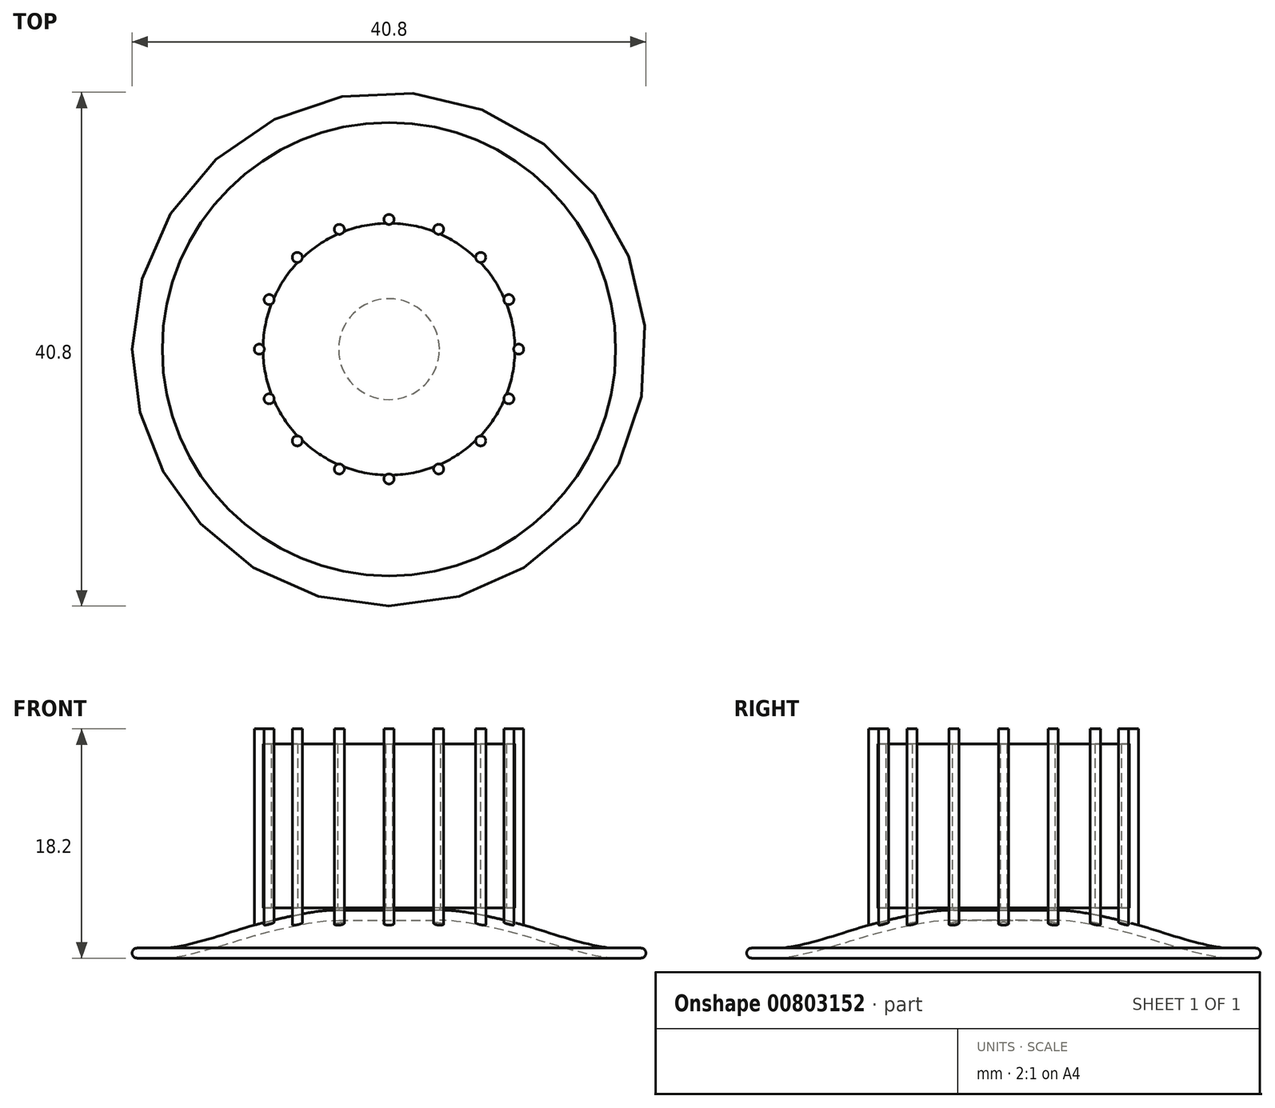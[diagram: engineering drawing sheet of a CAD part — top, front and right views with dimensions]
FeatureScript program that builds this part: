
annotation { "Feature Type Name" : "Feature", "Feature Type Description" : "" }
export const myFeature = defineFeature(function(context is Context, id is Id, definition is map)
    precondition{}
    {
        {
            var Q0;
            Q0=qCreatedBy(makeId("Right.planeOp"),FACE);
            var sketch = newSketch(context, id + "F0", { "sketchPlane" : qUnion([Q0])});
            skPoint(sketch, "E0", {"position": v(0, 3) * mm});
            skPoint(sketch, "E1", {"position": v(-4, 3) * mm});
            skPoint(sketch, "E2", {"position": v(-18, 0) * mm});
            skLineSegment(sketch, "E3", {"start": v(-4, 3) * mm, "end": v(0, 3) * mm});
            skLineSegment(sketch, "E4", {"start": v(-18, 0) * mm, "end": v(-20, 0) * mm});
            skFitSpline(sketch, "E5", {"points": [v(-18, 0) * mm, v(-14.38, 0.68) * mm, v(-10.9, 1.72) * mm, v(-7.39, 2.59) * mm, v(-4, 3) * mm], "startDerivative": vector(11.3, 0) * mm, "endDerivative": vector(14.02, 0) * mm});
            skLineSegment(sketch, "E6.bottom", {"start": v(0, 3) * mm, "end": v(-4, 3) * mm});
            skLineSegment(sketch, "E6.top", {"start": v(0, 4) * mm, "end": v(-4, 4) * mm});
            skLineSegment(sketch, "E6.left", {"start": v(0, 3) * mm, "end": v(0, 4) * mm});
            skLineSegment(sketch, "E6.right", {"start": v(-4, 3) * mm, "end": v(-4, 4) * mm});
            skPoint(sketch, "E7", {"position": v(-20, 0.8) * mm});
            skArc(sketch, "E8", {"start": v(-20, 0.8) * mm, "mid": v(-20.4, 0.4) * mm, "end": v(-20, 0) * mm});
            skFitSpline(sketch, "E9.0", {"points": [v(-18, 0.8) * mm, v(-17.81, 0.8) * mm, v(-17.35, 0.83) * mm, v(-16.22, 1.03) * mm, v(-14.61, 1.43) * mm, v(-12.89, 1.95) * mm, v(-11.2, 2.47) * mm, v(-9.43, 2.95) * mm, v(-7.93, 3.3) * mm, v(-6.74, 3.53) * mm, v(-5.55, 3.72) * mm, v(-4.63, 3.8) * mm, v(-4, 3.8) * mm]});
            skLineSegment(sketch, "E9.1", {"start": v(-18, 0.8) * mm, "end": v(-20, 0.8) * mm});
            skLineSegment(sketch, "E10.bottom", {"start": v(0, 4) * mm, "end": v(-10, 4) * mm});
            skLineSegment(sketch, "E10.top", {"start": v(0, 17) * mm, "end": v(-10, 17) * mm});
            skLineSegment(sketch, "E10.left", {"start": v(0, 4) * mm, "end": v(0, 17) * mm});
            skLineSegment(sketch, "E10.right", {"start": v(-10, 4) * mm, "end": v(-10, 17) * mm});
            skPoint(sketch, "E11", {"position": v(-10, 2.2) * mm});
            skPoint(sketch, "E12", {"position": v(-10.8, 2.2) * mm});
            skSolve(sketch);
        }
        {
            var Q0;
            Q0=makeQuery(id+"F0.imprint","IMPRINT",FACE,{"disambiguationData":[TD([[makeQuery(id+"F0.imprint","IMPRINT",EDGE,{"derivedFrom":sQuery(id+"F0.wireOp",EDGE,"E4")}),-1.0]])]});
            var Q1;
            {var subQ2=sQuery(id+"F0.wireOp",EDGE,"E3");Q1=makeQuery(id+"F0.imprint","IMPRINT",FACE,{"disambiguationData":[TD([[makeQuery(id+"F0.imprint","IMPRINT",EDGE,{"derivedFrom":subQ2}),1.0]])]});}
            var Q2;
            Q2=makeQuery(id+"F0.imprint","IMPRINT",FACE,{"disambiguationData":[TD([[makeQuery(id+"F0.imprint","IMPRINT",EDGE,{"derivedFrom":sQuery(id+"F0.wireOp",EDGE,"E6.top")}),-1.0]])]});
            var Q3;
            Q3=sQuery(id+"F0.wireOp",EDGE,"E6.left");
            revolve(context, id + "F1", {"surfaceOperationType" : NewSurfaceOperationType.NEW, "entities" : qUnion([Q0, Q1, Q2]), "axis" : qUnion([Q3]), "revolveType" : RevolveType.FULL});
        }
        {
            var Q0;
            Q0=qCreatedBy(makeId("Top.planeOp"),FACE);
            cPlane(context, id + "F2", {"entities" : qUnion([Q0]), "cplaneType" : CPlaneType.OFFSET, "offset" : 2.2 * mm, "width" : 150 * mm, "height" : 150 * mm});
        }
        {
            var Q0;
            Q0=qCreatedBy(id+"F2.planeOp",FACE);
            var sketch = newSketch(context, id + "F3", { "sketchPlane" : qUnion([Q0])});
            skPoint(sketch, "E13", {"position": v(-10.3, 0) * mm});
            skCircle(sketch, "E14", {"center": v(-10.3, 0) * mm, "radius": 0.4 * mm});
            skPoint(sketch, "E15.1.0", {"position": v(-9.52, -3.94) * mm});
            skCircle(sketch, "E15.1.1", {"center": v(-9.52, -3.94) * mm, "radius": 0.4 * mm});
            skPoint(sketch, "E15.2.0", {"position": v(-7.28, -7.28) * mm});
            skCircle(sketch, "E15.2.1", {"center": v(-7.28, -7.28) * mm, "radius": 0.4 * mm});
            skPoint(sketch, "E15.3.0", {"position": v(-3.94, -9.52) * mm});
            skCircle(sketch, "E15.3.1", {"center": v(-3.94, -9.52) * mm, "radius": 0.4 * mm});
            skPoint(sketch, "E15.4.0", {"position": v(0, -10.3) * mm});
            skCircle(sketch, "E15.4.1", {"center": v(0, -10.3) * mm, "radius": 0.4 * mm});
            skPoint(sketch, "E15.5.0", {"position": v(3.94, -9.52) * mm});
            skCircle(sketch, "E15.5.1", {"center": v(3.94, -9.52) * mm, "radius": 0.4 * mm});
            skPoint(sketch, "E15.6.0", {"position": v(7.28, -7.28) * mm});
            skCircle(sketch, "E15.6.1", {"center": v(7.28, -7.28) * mm, "radius": 0.4 * mm});
            skPoint(sketch, "E15.7.0", {"position": v(9.52, -3.94) * mm});
            skCircle(sketch, "E15.7.1", {"center": v(9.52, -3.94) * mm, "radius": 0.4 * mm});
            skPoint(sketch, "E15.8.0", {"position": v(10.3, 0) * mm});
            skCircle(sketch, "E15.8.1", {"center": v(10.3, 0) * mm, "radius": 0.4 * mm});
            skPoint(sketch, "E15.9.0", {"position": v(9.52, 3.94) * mm});
            skCircle(sketch, "E15.9.1", {"center": v(9.52, 3.94) * mm, "radius": 0.4 * mm});
            skPoint(sketch, "E15.10.0", {"position": v(7.28, 7.28) * mm});
            skCircle(sketch, "E15.10.1", {"center": v(7.28, 7.28) * mm, "radius": 0.4 * mm});
            skPoint(sketch, "E15.11.0", {"position": v(3.94, 9.52) * mm});
            skCircle(sketch, "E15.11.1", {"center": v(3.94, 9.52) * mm, "radius": 0.4 * mm});
            skPoint(sketch, "E15.12.0", {"position": v(0, 10.3) * mm});
            skCircle(sketch, "E15.12.1", {"center": v(0, 10.3) * mm, "radius": 0.4 * mm});
            skPoint(sketch, "E15.13.0", {"position": v(-3.94, 9.52) * mm});
            skCircle(sketch, "E15.13.1", {"center": v(-3.94, 9.52) * mm, "radius": 0.4 * mm});
            skPoint(sketch, "E15.14.0", {"position": v(-7.28, 7.28) * mm});
            skCircle(sketch, "E15.14.1", {"center": v(-7.28, 7.28) * mm, "radius": 0.4 * mm});
            skPoint(sketch, "E15.15.0", {"position": v(-9.52, 3.94) * mm});
            skCircle(sketch, "E15.15.1", {"center": v(-9.52, 3.94) * mm, "radius": 0.4 * mm});
            skPoint(sketch, "E15.center", {"position": v(0, 0) * mm});
            skSolve(sketch);
        }
        {
            var Q0;
            Q0 = qSketchRegion(id + "F3", true);
            extrude(context, id + "F4", {"entities" : qUnion([Q0]), "operationType" : NewBodyOperationType.ADD, "depth" : 16 * mm, "offsetDistance" : 25 * mm});
        }
    });
